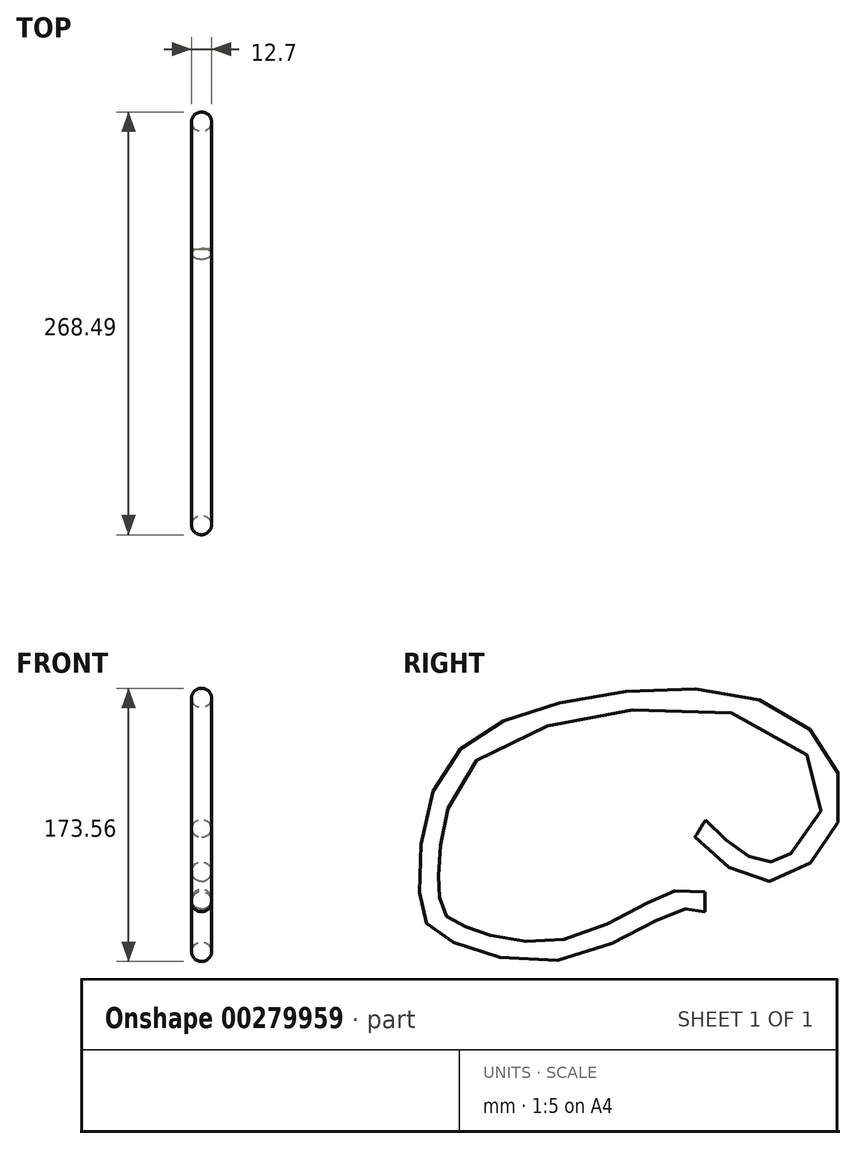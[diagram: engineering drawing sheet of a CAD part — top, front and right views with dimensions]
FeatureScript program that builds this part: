
annotation { "Feature Type Name" : "Feature", "Feature Type Description" : "" }
export const myFeature = defineFeature(function(context is Context, id is Id, definition is map)
    precondition{}
    {
        {
            var Q0;
            Q0=qCreatedBy(makeId("Right.planeOp"),FACE);
            var sketch = newSketch(context, id + "F0", { "sketchPlane" : qUnion([Q0])});
            skPoint(sketch, "E0.1.internal.orphan", {"position": v(-20.07, 0) * mm});
            skPoint(sketch, "E0.11.internal.orphan", {"position": v(0, 35.88) * mm});
            skPoint(sketch, "E0.12.internal.orphan", {"position": v(0, 30.5) * mm});
            skPoint(sketch, "E0.6.internal.orphan", {"position": v(-174.77, 0) * mm});
            skFitSpline(sketch, "E1", {"points": [v(0, 0) * mm, v(-20.07, 0) * mm, v(-92.3, -30.84) * mm, v(-166.7, -15.12) * mm, v(-174.77, 0) * mm, v(-163.97, 74.56) * mm, v(-96.92, 118.78) * mm, v(42.85, 118.15) * mm, v(80.15, 59.27) * mm, v(42.43, 19.24) * mm, v(-3.04, 46.48) * mm], "startDerivative": vector(-309.54, 70.66) * mm, "endDerivative": vector(-475.68, 469.04) * mm});
            skSolve(sketch);
        }
        {
            var Q0;
            Q0=qCreatedBy(makeId("Front.planeOp"),FACE);
            var sketch = newSketch(context, id + "F1", { "sketchPlane" : qUnion([Q0])});
            skCircle(sketch, "E2", {"center": v(0, 0) * mm, "radius": 6.35 * mm});
            skSolve(sketch);
        }
        {
            var Q0;
            Q0=makeQuery(id+"F1.imprint","IMPRINT",FACE,{"disambiguationData":[TD([[makeQuery(id+"F1.imprint","IMPRINT",EDGE,{"derivedFrom":sQuery(id+"F1.wireOp",EDGE,"E2")}),1.0]])]});
            var Q1;
            Q1=sQuery(id+"F0.wireOp",EDGE,"E1");
            sweep(context, id + "F2", {"profiles" : qUnion([Q0]), "path" : qUnion([Q1])});
        }
    });
